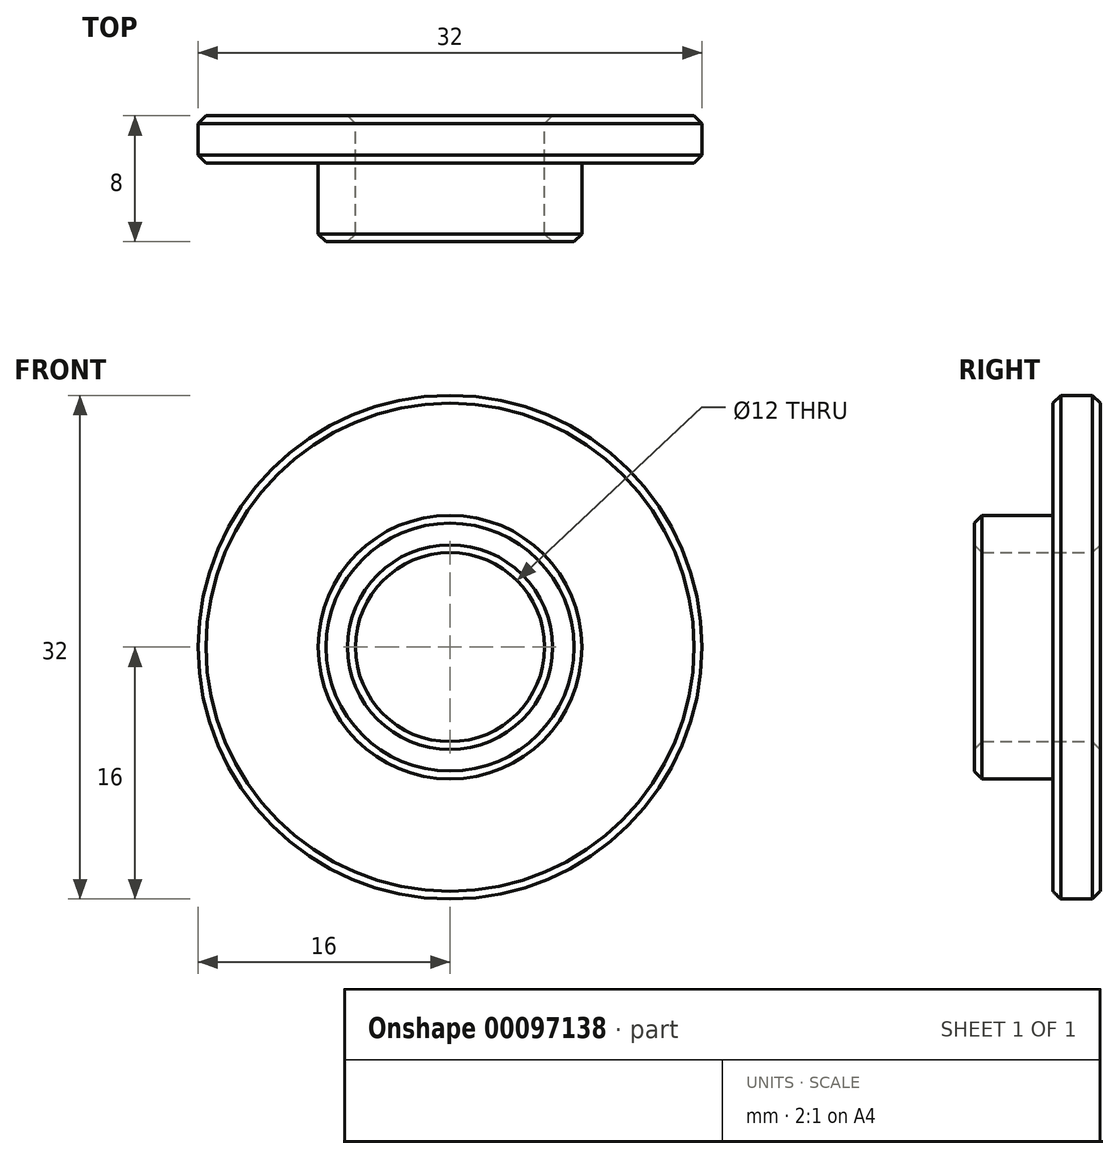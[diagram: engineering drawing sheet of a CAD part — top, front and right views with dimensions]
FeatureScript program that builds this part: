
annotation { "Feature Type Name" : "Feature", "Feature Type Description" : "" }
export const myFeature = defineFeature(function(context is Context, id is Id, definition is map)
    precondition{}
    {
        {
            var Q0;
            Q0=qCreatedBy(makeId("Front.planeOp"),FACE);
            var sketch = newSketch(context, id + "F0", { "sketchPlane" : qUnion([Q0])});
            skCircle(sketch, "E0", {"center": v(0, 0) * mm, "radius": 16 * mm});
            skCircle(sketch, "E1", {"center": v(0, 0) * mm, "radius": 8.38 * mm});
            skCircle(sketch, "E2", {"center": v(0, 0) * mm, "radius": 6 * mm});
            skSolve(sketch);
        }
        {
            var Q0;
            Q0=makeQuery(id+"F0.imprint","IMPRINT",FACE,{"disambiguationData":[TD([[makeQuery(id+"F0.imprint","IMPRINT",EDGE,{"derivedFrom":sQuery(id+"F0.wireOp",EDGE,"E0")}),1.0]])]});
            var Q1;
            Q1=makeQuery(id+"F0.imprint","IMPRINT",FACE,{"disambiguationData":[TD([[makeQuery(id+"F0.imprint","IMPRINT",EDGE,{"derivedFrom":sQuery(id+"F0.wireOp",EDGE,"E1")}),1.0]])]});
            extrude(context, id + "F1", {"entities" : qUnion([Q0, Q1]), "depth" : 3 * mm});
        }
        {
            var Q0;
            Q0=makeQuery(id+"F0.imprint","IMPRINT",FACE,{"disambiguationData":[TD([[makeQuery(id+"F0.imprint","IMPRINT",EDGE,{"derivedFrom":sQuery(id+"F0.wireOp",EDGE,"E1")}),1.0]])]});
            extrude(context, id + "F2", {"entities" : qUnion([Q0]), "operationType" : NewBodyOperationType.ADD, "depth" : 8 * mm});
        }
        {
            var Q0;
            Q0=makeQuery(id+"F1.opExtrude","SWEPT_FACE",FACE,{"disambiguationData":[OSD([sQuery(id+"F0.wireOp",EDGE,"E0")])]});
            var Q1;
            {var subQ0=sQuery(id+"F0.wireOp",EDGE,"E2");Q1=makeQuery(id+"F2.boolean.opBoolean","MERGE",FACE,{"derivedFrom":[makeQuery(id+"F1.opExtrude","SWEPT_FACE",FACE,{"disambiguationData":[OSD([subQ0])]}),makeQuery(id+"F2.opExtrude","SWEPT_FACE",FACE,{"disambiguationData":[OSD([subQ0])]})]});}
            var Q2;
            Q2=makeQuery(id+"F2.opExtrude","CAP_EDGE",EDGE,{"disambiguationData":[OSD([sQuery(id+"F0.wireOp",EDGE,"E1")])],"isStart":false});
            chamfer(context, id + "F3", {"entities" : qUnion([Q0, Q1, Q2]), "width" : 0.5 * mm, "tangentPropagation" : true});
        }
    });
